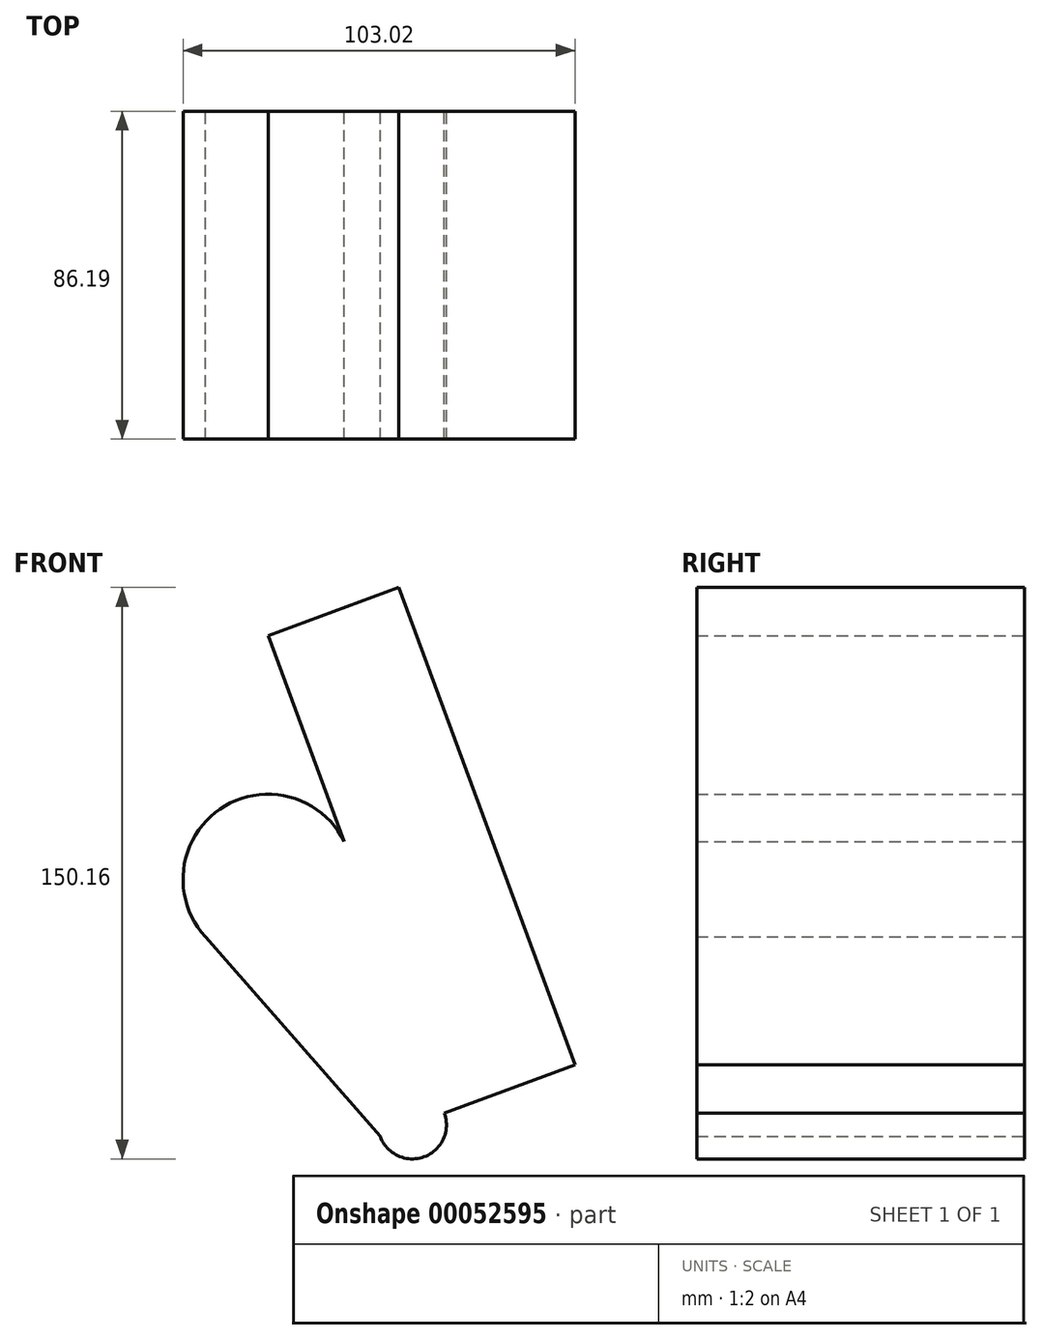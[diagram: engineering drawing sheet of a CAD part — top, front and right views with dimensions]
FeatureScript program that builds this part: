
annotation { "Feature Type Name" : "Feature", "Feature Type Description" : "" }
export const myFeature = defineFeature(function(context is Context, id is Id, definition is map)
    precondition{}
    {
        {
            var Q0;
            Q0=qCreatedBy(makeId("Front.planeOp"),FACE);
            var sketch = newSketch(context, id + "F0", { "sketchPlane" : qUnion([Q0])});
            skArc(sketch, "E0", {"start": v(-45.06, 63.16) * mm, "mid": v(-77.33, 77.35) * mm, "end": v(-83.2, 42.59) * mm});
            skArc(sketch, "E1", {"start": v(-37.25, -9.88) * mm, "mid": v(-25.73, -15.26) * mm, "end": v(-20.39, -3.72) * mm});
            skLineSegment(sketch, "E2", {"start": v(-45.06, 63.16) * mm, "end": v(-21.76, 0) * mm});
            skLineSegment(sketch, "E3", {"start": v(-83.2, 42.59) * mm, "end": v(-37.25, -9.88) * mm});
            skLineSegment(sketch, "E4", {"start": v(-21.76, 0) * mm, "end": v(-20.39, -3.72) * mm});
            skSolve(sketch);
        }
        {
            var Q0;
            Q0=makeQuery(id+"F0.imprint","IMPRINT",FACE,{"disambiguationData":[TD([[makeQuery(id+"F0.imprint","IMPRINT",EDGE,{"derivedFrom":sQuery(id+"F0.wireOp",EDGE,"E0")}),1.0]])]});
            extrude(context, id + "F1", {"entities" : qUnion([Q0]), "depth" : 86.2 * mm});
        }
        {
            var Q0;
            Q0=makeQuery(id+"F1.opExtrude","SWEPT_FACE",FACE,{"disambiguationData":[OSD([sQuery(id+"F0.wireOp",EDGE,"E2"),sQuery(id+"F0.wireOp",EDGE,"E4")])]});
            extrude(context, id + "F2", {"entities" : qUnion([Q0]), "operationType" : NewBodyOperationType.ADD, "depth" : 36.6 * mm});
        }
        {
            var Q0;
            Q0=makeQuery(id+"F1.opExtrude","SWEPT_FACE",FACE,{"disambiguationData":[OSD([sQuery(id+"F0.wireOp",EDGE,"E2"),sQuery(id+"F0.wireOp",EDGE,"E4")])]});
            var Q1;
            Q1=makeQuery(id+"F2.opExtrude","SWEPT_FACE",FACE,{"disambiguationData":[OSD([sQuery(id+"F0.wireOp",EDGE,"E0"),sQuery(id+"F0.wireOp",EDGE,"E2")])]});
            extrude(context, id + "F3", {"entities" : qUnion([Q0, Q1]), "operationType" : NewBodyOperationType.ADD, "depth" : 62.4 * mm});
        }
    });
